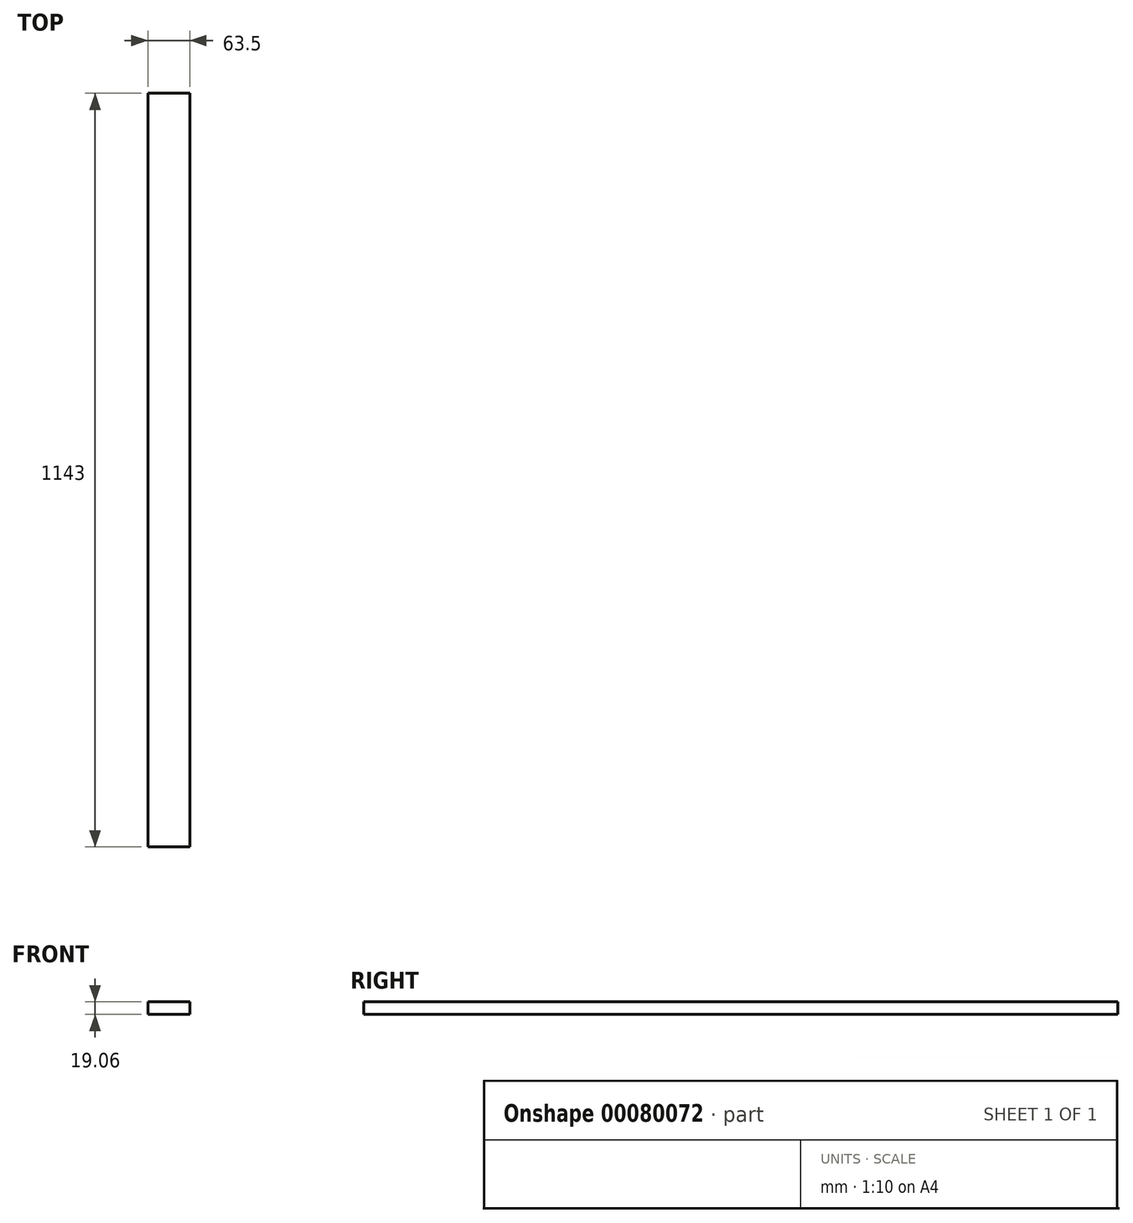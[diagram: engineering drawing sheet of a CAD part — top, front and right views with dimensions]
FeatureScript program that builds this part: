
annotation { "Feature Type Name" : "Feature", "Feature Type Description" : "" }
export const myFeature = defineFeature(function(context is Context, id is Id, definition is map)
    precondition{}
    {
        {
            var Q0;
            Q0=qCreatedBy(makeId("Front.planeOp"),FACE);
            var sketch = newSketch(context, id + "F0", { "sketchPlane" : qUnion([Q0])});
            skLineSegment(sketch, "E0.bottom", {"start": v(-31.75, 9.52) * mm, "end": v(31.75, 9.52) * mm});
            skLineSegment(sketch, "E0.top", {"start": v(-31.75, -9.52) * mm, "end": v(31.75, -9.52) * mm});
            skLineSegment(sketch, "E0.left", {"start": v(-31.75, 9.52) * mm, "end": v(-31.75, -9.53) * mm});
            skLineSegment(sketch, "E0.right", {"start": v(31.75, 9.52) * mm, "end": v(31.75, -9.52) * mm});
            skPoint(sketch, "E0.middle", {"position": v(0, 0) * mm});
            skSolve(sketch);
        }
        {
            var Q0;
            Q0 = qSketchRegion(id + "F0", true);
            extrude(context, id + "F1", {"entities" : qUnion([Q0]), "endBound" : BoundingType.SYMMETRIC, "depth" : 1143 * mm});
        }
    });
